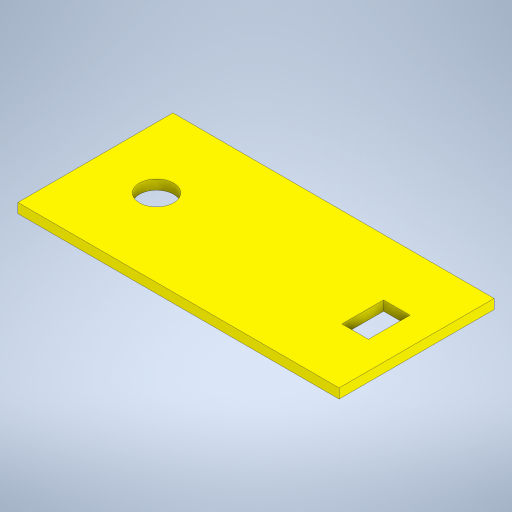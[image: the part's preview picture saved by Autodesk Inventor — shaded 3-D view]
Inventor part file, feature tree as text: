
AUTODESK INVENTOR PART (.ipt)
format: ipt  version: 2024 (Build 280153000, 153)  size: 241,152 bytes
history: native  units: mm
features: extrude x3, sketch x3
ambient origin geometry x8: Origin, YZ Plane, XZ Plane, XY Plane, X Axis, Y Axis, Z Axis, Center Point
bodies: Solid1 (feature_tree)
feature tree (6):
  extrude  "Extrusion1"  Depth=50.0mm
  extrude  "Extrusion2"  Depth=3.125mm
  extrude  "Extrusion3"  Depth=8.5mm
  sketch  "Sketch1"  dims[d0=103.6mm d1=50.0mm]
  sketch  "Sketch2"  dims[d2=3.125mm d3=0.0mm d4=11.0mm]
  sketch  "Sketch3"  dims[d5=3.125mm d6=0.0mm d7=8.5mm d8=13.4mm d9=3.125mm d10=0.0mm]
